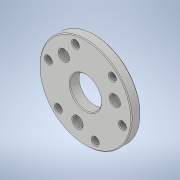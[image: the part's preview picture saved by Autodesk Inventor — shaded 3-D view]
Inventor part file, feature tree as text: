
AUTODESK INVENTOR PART (.ipt)
format: ipt  version: 2021 (Build 250183000, 183)  size: 174,592 bytes
history: native  units: in
note: dims shown in document units (in); Inventor stores cm internally (conversion verified against a paired STEP export)
features: sketch x3, extrude x2, revolve x1, chamfer x1
ambient origin geometry x8: Origin, YZ Plane, XZ Plane, XY Plane, X Axis, Y Axis, Z Axis, Center Point
bodies: Solid1 (feature_tree)
feature tree (7):
  revolve  "Revolution1"  [1 undecoded]
  extrude  "Extrusion1"  Depth=3.078in
  extrude  "Extrusion2"  Depth=0.375in
  chamfer  "Chamfer1"  Distance=2.3622in Angle=360.0deg
  sketch  "Sketch1"  dims[d0=1.8505in d1=0.375in]
  sketch  "Sketch2"  dims[d2=90.0deg d3=3.078in]
  sketch  "Sketch3"  dims[d4=45.0deg d5=0.268in d6=2.3622in d8=360.0deg d10=0.375in d11=0.0in d12=2.451in d13=135.0deg d14=0.4in d15=1.1811in d17=360.0deg d19=0.375in d20=0.0in d21=1.25in d22=0.03in d23=0.125in d24=45.0deg]
note: 1 required parameter value undecoded (feature->parameter linkage not recoverable at this tier; creation-order binding heuristic only, values carry confidence <= 0.55)
